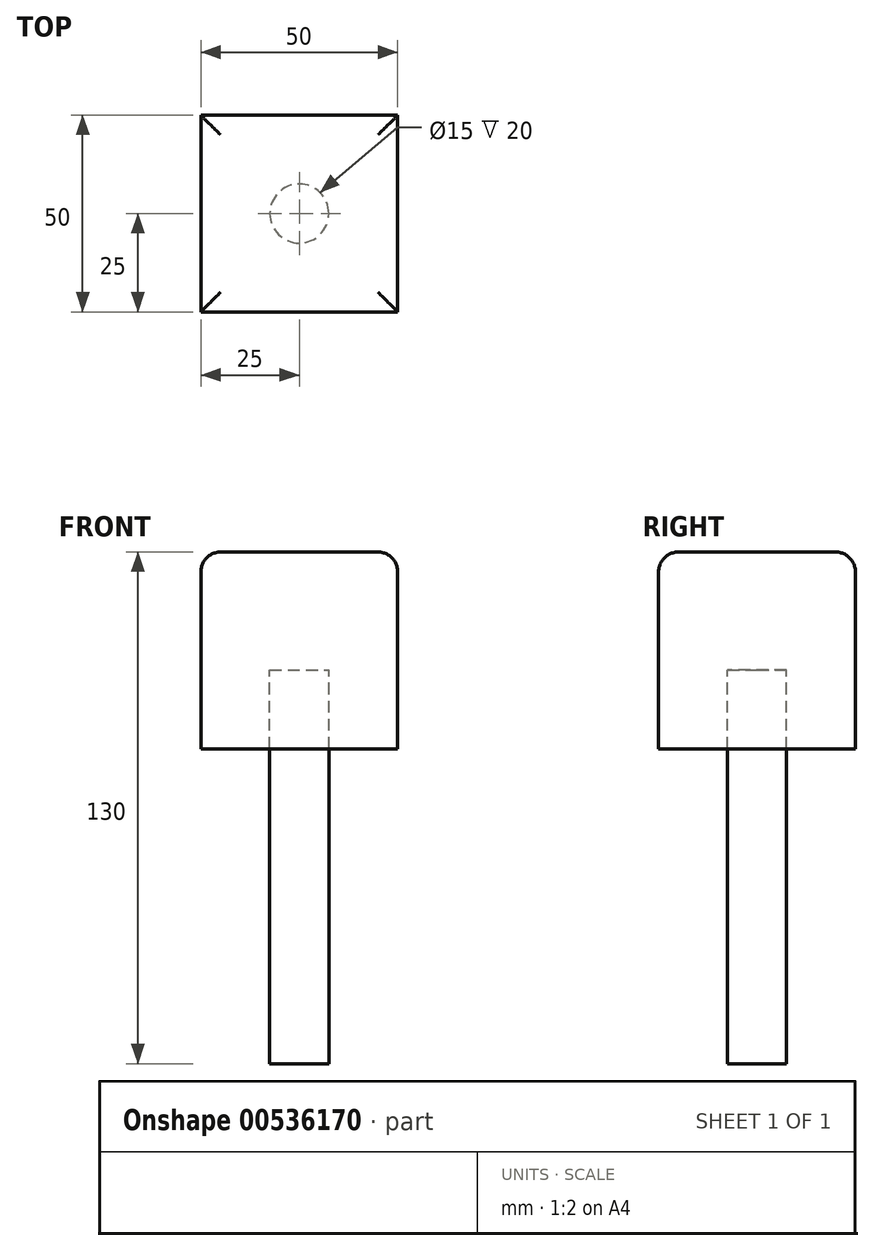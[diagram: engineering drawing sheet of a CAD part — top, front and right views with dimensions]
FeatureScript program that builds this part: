
annotation { "Feature Type Name" : "Feature", "Feature Type Description" : "" }
export const myFeature = defineFeature(function(context is Context, id is Id, definition is map)
    precondition{}
    {
        {
            var Q0;
            Q0=qCreatedBy(makeId("Top.planeOp"),FACE);
            var sketch = newSketch(context, id + "F0", { "sketchPlane" : qUnion([Q0])});
            skLineSegment(sketch, "E0.bottom", {"start": v(25, -25) * mm, "end": v(-25, -25) * mm});
            skLineSegment(sketch, "E0.top", {"start": v(25, 25) * mm, "end": v(-25, 25) * mm});
            skLineSegment(sketch, "E0.left", {"start": v(25, -25) * mm, "end": v(25, 25) * mm});
            skLineSegment(sketch, "E0.right", {"start": v(-25, -25) * mm, "end": v(-25, 25) * mm});
            skPoint(sketch, "E1.middle", {"position": v(0, 0) * mm});
            skSolve(sketch);
        }
        {
            var Q0;
            Q0=makeQuery(id+"F0.imprint","IMPRINT",FACE,{"disambiguationData":[TD([[makeQuery(id+"F0.imprint","IMPRINT",EDGE,{"derivedFrom":sQuery(id+"F0.wireOp",EDGE,"E0.bottom")}),-1.0]])]});
            extrude(context, id + "F1", {"entities" : qUnion([Q0]), "depth" : 50 * mm, "offsetDistance" : 25 * mm});
        }
        {
            var Q0;
            Q0=makeQuery(id+"F1.opExtrude","CAP_EDGE",EDGE,{"disambiguationData":[OSD([sQuery(id+"F0.wireOp",EDGE,"E0.left")])],"isStart":false});
            var Q1;
            Q1=makeQuery(id+"F1.opExtrude","CAP_EDGE",EDGE,{"disambiguationData":[OSD([sQuery(id+"F0.wireOp",EDGE,"E0.top")])],"isStart":false});
            var Q2;
            Q2=makeQuery(id+"F1.opExtrude","CAP_EDGE",EDGE,{"disambiguationData":[OSD([sQuery(id+"F0.wireOp",EDGE,"E0.right")])],"isStart":false});
            var Q3;
            Q3=makeQuery(id+"F1.opExtrude","CAP_EDGE",EDGE,{"disambiguationData":[OSD([sQuery(id+"F0.wireOp",EDGE,"E0.bottom")])],"isStart":false});
            fillet(context, id + "F2", {"entities" : qUnion([Q0, Q1, Q2, Q3]), "radius" : 5 * mm, "tangentPropagation" : true, "allowEdgeOverflow" : false});
        }
        {
            var Q0;
            Q0=makeQuery(id+"F1.opExtrude","CAP_FACE",FACE,{"disambiguationData":[OSD([sQuery(id+"F0.wireOp",EDGE,"E0.bottom"),sQuery(id+"F0.wireOp",EDGE,"E0.top"),sQuery(id+"F0.wireOp",EDGE,"E0.left"),sQuery(id+"F0.wireOp",EDGE,"E0.right")])],"isStart":true});
            var sketch = newSketch(context, id + "F3", { "sketchPlane" : qUnion([Q0])});
            skCircle(sketch, "E2", {"center": v(0, 0) * mm, "radius": 7.5 * mm});
            skSolve(sketch);
        }
        {
            var Q0;
            Q0=makeQuery(id+"F3.imprint","IMPRINT",FACE,{"disambiguationData":[TD([[makeQuery(id+"F3.imprint","IMPRINT",EDGE,{"derivedFrom":sQuery(id+"F3.wireOp",EDGE,"E2")}),1.0]])]});
            var Q1;
            Q1=sQuery(id+"F3.wireOp",EDGE,"E2");
            extrude(context, id + "F4", {"entities" : qUnion([Q0]), "operationType" : NewBodyOperationType.REMOVE, "surfaceEntities" : qUnion([Q1]), "oppositeDirection" : true, "depth" : 20 * mm, "offsetDistance" : 25 * mm});
        }
        {
            var Q0;
            Q0=makeQuery(id+"F4.boolean.opBoolean","COPY",FACE,{"derivedFrom":makeQuery(id+"F4.opExtrude","CAP_FACE",FACE,{"disambiguationData":[OSD([sQuery(id+"F3.wireOp",EDGE,"E2")])],"isStart":false})});
            extrude(context, id + "F5", {"entities" : qUnion([Q0]), "depth" : 100 * mm, "offsetDistance" : 25 * mm});
        }
    });
